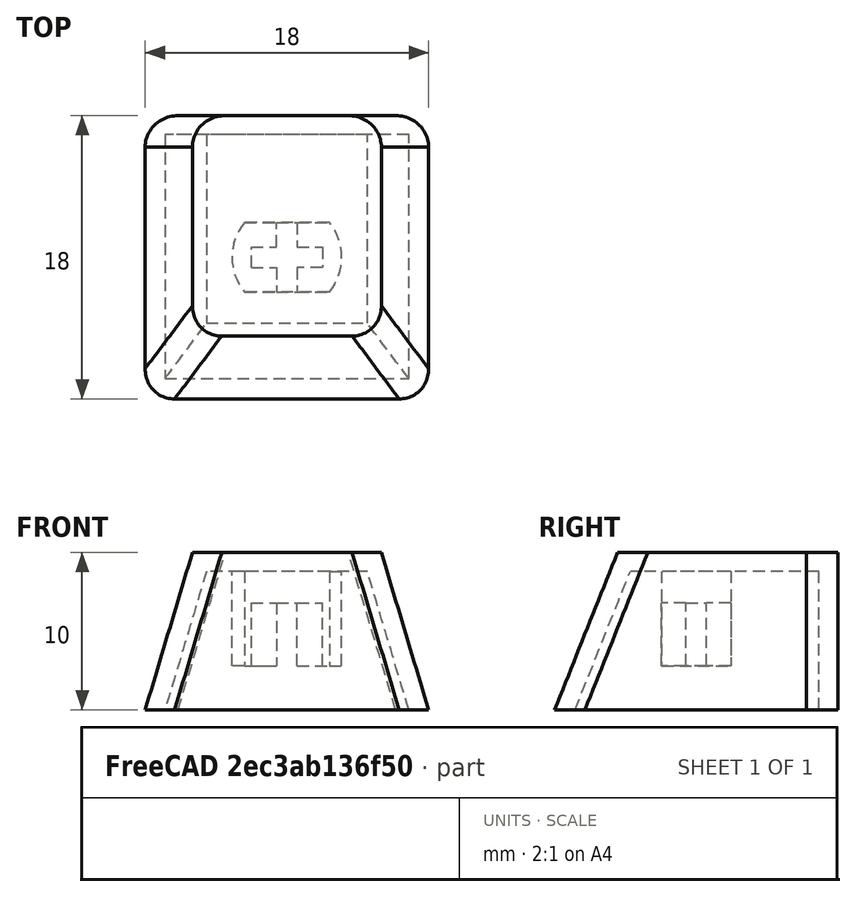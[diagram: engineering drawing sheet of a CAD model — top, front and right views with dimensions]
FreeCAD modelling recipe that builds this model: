
FCSTD DOCUMENT  (FreeCAD 0.19R19285 (Git))
Label: keycap4
Comment: 3D-parts by Obijuan -- https://github.com/Obijuan/3D-parts
License: CreativeCommons Attribution-ShareAlike
LicenseURL: http://creativecommons.org/licenses/by-sa/4.0/
objects: Sketcher::SketchObject×5, PartDesign::Plane×4, PartDesign::AdditiveLoft×1, PartDesign::Thickness×1, PartDesign::Pad×1, PartDesign::Pocket×1, PartDesign::Fillet×1, PartDesign::Body×1, Mesh::Feature×1, App::DocumentObjectGroup×1
note: 18 computed .brp shape members not serialized (recipe doc carries the construction recipe); baked Part::Feature solids carry a one-line shape summary decoded from their .brp

FEATURE [Sketcher::SketchObject] Sketch  label="master-h"
  MapMode = 5
  Support = -> [XY_Plane]
  sketch-geometry (4):
    g0: LineSegment StartX=-9 StartY=9 StartZ=0 EndX=9 EndY=9 EndZ=0
    g1: LineSegment StartX=9 StartY=9 StartZ=0 EndX=9 EndY=-9 EndZ=0
    g2: LineSegment StartX=9 StartY=-9 StartZ=0 EndX=-9 EndY=-9 EndZ=0
    g3: LineSegment StartX=-9 StartY=-9 StartZ=0 EndX=-9 EndY=9 EndZ=0
  constraints (10):
    c: Coincident(g0,g1)
    c: Coincident(g1,g2)
    c: Coincident(g2,g3)
    c: Coincident(g3,g0)
    c: Horizontal(g2)
    c: Vertical(g1)
    c: Symmetric(g0,g2,g-1)
    c: Symmetric(g0,g0,g-2)
    c: DistanceX(g0,g0) = 18
    c: Equal(g0,g3)
FEATURE [PartDesign::Plane] DatumPlane  label="top-plane"
  AttachmentOffset = pos=(0,0,10) rot=(0,0,1;0rad)
  Length = 60
  MapMode = 5
  Placement = pos=(0,0,10) rot=(0,0,1;0rad)
  ResizeMode = 0
  Support = -> [XY_Plane]
  Width = 60
FEATURE [Sketcher::SketchObject] Sketch001  label="key-top-sketch"
  ExternalGeometry = -> [Sketch]
  MapMode = 5
  Placement = pos=(0,0,10) rot=(0,0,1;0rad)
  Support = -> [DatumPlane]
  sketch-geometry (4):
    g0: LineSegment StartX=-6 StartY=9 StartZ=0 EndX=6 EndY=9 EndZ=0
    g1: LineSegment StartX=6 StartY=9 StartZ=0 EndX=6 EndY=-5 EndZ=0
    g2: LineSegment StartX=6 StartY=-5 StartZ=0 EndX=-6 EndY=-5 EndZ=0
    g3: LineSegment StartX=-6 StartY=-5 StartZ=0 EndX=-6 EndY=9 EndZ=0
  constraints (11):
    c: Coincident(g0,g1)
    c: Coincident(g1,g2)
    c: Coincident(g2,g3)
    c: Coincident(g3,g0)
    c: Horizontal(g2)
    c: Vertical(g1)
    c: Vertical(g3)
    c: DistanceY(g1,g1) = 14
    c: Symmetric(g0,g0,g-2)
    c: PointOnObject(g0,g-3)
    c: DistanceX(g0,g0) = 12
FEATURE [PartDesign::Plane] DatumPlane001  label="base-plane"
  Length = 60
  MapMode = 5
  ResizeMode = 0
  Support = -> [XY_Plane]
  Width = 60
FEATURE [Sketcher::SketchObject] Sketch002  label="key-bottom-sketch"
  ExternalGeometry = -> [Sketch]
  MapMode = 5
  sketch-geometry (4):
    g0: LineSegment StartX=-9 StartY=9 StartZ=0 EndX=9 EndY=9 EndZ=0
    g1: LineSegment StartX=9 StartY=9 StartZ=0 EndX=9 EndY=-9 EndZ=0
    g2: LineSegment StartX=9 StartY=-9 StartZ=0 EndX=-9 EndY=-9 EndZ=0
    g3: LineSegment StartX=-9 StartY=-9 StartZ=0 EndX=-9 EndY=9 EndZ=0
  constraints (10):
    c: Coincident(g0,g1)
    c: Coincident(g1,g2)
    c: Coincident(g2,g3)
    c: Coincident(g3,g0)
    c: Horizontal(g0)
    c: Horizontal(g2)
    c: Vertical(g1)
    c: Vertical(g3)
    c: Coincident(g1,g-4)
    c: Coincident(g0,g-3)
FEATURE [PartDesign::AdditiveLoft] AdditiveLoft  label="key-body"
  Closed = false
  Profile = -> Sketch002
  Refine = true
  Ruled = false
  Sections = -> [Sketch001]
FEATURE [PartDesign::Plane] DatumPlane002  label="top-inner-plane"
  AttachmentOffset = pos=(0,0,9.8) rot=(0,0,1;0rad)
  Length = 60
  MapMode = 5
  Placement = pos=(0,0,9.8) rot=(0,0,1;0rad)
  ResizeMode = 0
  Support = -> [XY_Plane]
  Width = 60
  expr: .AttachmentOffset.Base.z = 11 - 1.2
FEATURE [Sketcher::SketchObject] Sketch006  label="inner-support-sk"
  MapMode = 5
  Placement = pos=(0,0,9.8) rot=(0,0,1;0rad)
  Support = -> [DatumPlane002]
  sketch-geometry (5):
    g0: ArcOfCircle CenterX=0 CenterY=0 CenterZ=0 NormalX=0 NormalY=0 NormalZ=1 AngleXU=0 Radius=3.48281 StartAngle=2.45788 EndAngle=3.8253
    g1: LineSegment [constr] StartX=-2.7 StartY=2.2 StartZ=0 EndX=-2.7 EndY=-2.2 EndZ=0
    g2: LineSegment StartX=-2.7 StartY=2.2 StartZ=0 EndX=2.7 EndY=2.2 EndZ=0
    g3: LineSegment StartX=-2.7 StartY=-2.2 StartZ=0 EndX=2.7 EndY=-2.2 EndZ=0
    g4: ArcOfCircle CenterX=0 CenterY=0 CenterZ=0 NormalX=0 NormalY=0 NormalZ=1 AngleXU=0 Radius=3.48281 StartAngle=5.59948 EndAngle=6.96689
  constraints (13):
    c: Coincident(g0,g-1)
    c: Coincident(g1,g0)
    c: Coincident(g1,g0)
    c: Vertical(g1)
    c: DistanceY(g1,g1) = 4.4
    c: Coincident(g2,g0)
    c: DistanceX(g2,g2) = 5.4
    c: Symmetric(g0,g2,g-2)
    c: Coincident(g3,g0)
    c: Coincident(g4,g0)
    c: Coincident(g4,g3)
    c: Coincident(g4,g2)
    c: Horizontal(g3)
FEATURE [PartDesign::Plane] DatumPlane003  label="inner-support-base"
  AttachmentOffset = pos=(0,0,2.8) rot=(0,0,1;0rad)
  Length = 60
  MapMode = 5
  Placement = pos=(0,0,2.8) rot=(0,0,1;0rad)
  ResizeMode = 0
  Support = -> [XY_Plane]
  Width = 60
FEATURE [Sketcher::SketchObject] Sketch007  label="cross-sk"
  MapMode = 5
  Placement = pos=(0,0,2.8) rot=(0,0,1;0rad)
  Support = -> [DatumPlane003]
  sketch-geometry (12):
    g0: LineSegment StartX=-2.25 StartY=-0.65 StartZ=0 EndX=-2.25 EndY=0.65 EndZ=0
    g1: LineSegment StartX=-2.25 StartY=0.65 StartZ=0 EndX=-0.65 EndY=0.65 EndZ=0
    g2: LineSegment StartX=-0.65 StartY=0.65 StartZ=0 EndX=-0.65 EndY=2.25 EndZ=0
    g3: LineSegment StartX=-0.65 StartY=2.25 StartZ=0 EndX=0.65 EndY=2.25 EndZ=0
    g4: LineSegment StartX=-2.25 StartY=-0.65 StartZ=0 EndX=-0.65 EndY=-0.65 EndZ=0
    g5: LineSegment StartX=-0.65 StartY=-0.65 StartZ=0 EndX=-0.65 EndY=-2.25 EndZ=0
    g6: LineSegment StartX=-0.65 StartY=-2.25 StartZ=0 EndX=0.65 EndY=-2.25 EndZ=0
    g7: LineSegment StartX=0.65 StartY=2.25 StartZ=0 EndX=0.65 EndY=0.65 EndZ=0
    g8: LineSegment StartX=0.65 StartY=0.65 StartZ=0 EndX=2.25 EndY=0.65 EndZ=0
    g9: LineSegment StartX=2.25 StartY=0.65 StartZ=0 EndX=2.25 EndY=-0.65 EndZ=0
    g10: LineSegment StartX=2.25 StartY=-0.65 StartZ=0 EndX=0.65 EndY=-0.65 EndZ=0
    g11: LineSegment StartX=0.65 StartY=-0.65 StartZ=0 EndX=0.65 EndY=-2.25 EndZ=0
  constraints (27):
    c: Coincident(g0,g1)
    c: Horizontal(g1)
    c: Coincident(g1,g2)
    c: Vertical(g2)
    c: Coincident(g2,g3)
    c: DistanceX(g3,g3) = 1.3
    c: Symmetric(g2,g3,g-2)
    c: Equal(g0,g3)
    c: DistanceX(g1,g1) = 1.6
    c: Symmetric(g0,g0,g-1)
    c: Coincident(g4,g0)
    c: Symmetric(g4,g1,g-1)
    c: Coincident(g4,g5)
    c: Coincident(g5,g6)
    c: Symmetric(g5,g2,g-1)
    c: Symmetric(g6,g3,g-1)
    c: Coincident(g3,g7)
    c: Coincident(g7,g8)
    c: Coincident(g8,g9)
    c: Coincident(g9,g10)
    c: Coincident(g10,g11)
    c: Coincident(g11,g6)
    c: Symmetric(g1,g7,g-2)
    c: Symmetric(g4,g10,g-2)
    c: Symmetric(g9,g0,g-1)
    c: Symmetric(g0,g8,g-2)
    c: Equal(g7,g8)
FEATURE [PartDesign::Thickness] Thickness
  Base = -> AdditiveLoft [Face1]
  BaseFeature = -> AdditiveLoft
  Intersection = false
  Join = 1
  Mode = 0
  Reversed = true
  Value = 1.2
FEATURE [PartDesign::Pad] Pad001  label="Inner-support"
  BaseFeature = -> Thickness
  Length = 7
  Length2 = 100
  Profile = -> Sketch006
  Refine = true
  Reversed = true
  Type = 0
FEATURE [PartDesign::Pocket] Pocket001  label="cross-cutout"
  BaseFeature = -> Pad001
  Length = 4
  Length2 = 100
  Profile = -> Sketch007
  Refine = true
  Reversed = true
  Type = 0
FEATURE [PartDesign::Fillet] Fillet
  Base = -> Pocket001 [Edge12,Edge16,Edge4,Edge2]
  BaseFeature = -> Pocket001
  Radius = 2
FEATURE [PartDesign::Body] Body  label="Keycap"
  Group = -> [Sketch,DatumPlane,DatumPlane001,DatumPlane002,DatumPlane003,Sketch001,Sketch002,AdditiveLoft,Thickness,Sketch006,Pad001,Sketch007,Pocket001,Fillet]
  Origin = -> Origin
  Tip = -> Fillet
FEATURE [Mesh::Feature] Mesh  label="Keycap (Meshed)"
  Placement = pos=(-1.2e-15,0,10) rot=(0,1,0;3.14159rad)
FEATURE [App::DocumentObjectGroup] Group  label="Printing"
  Group = -> [Mesh]
